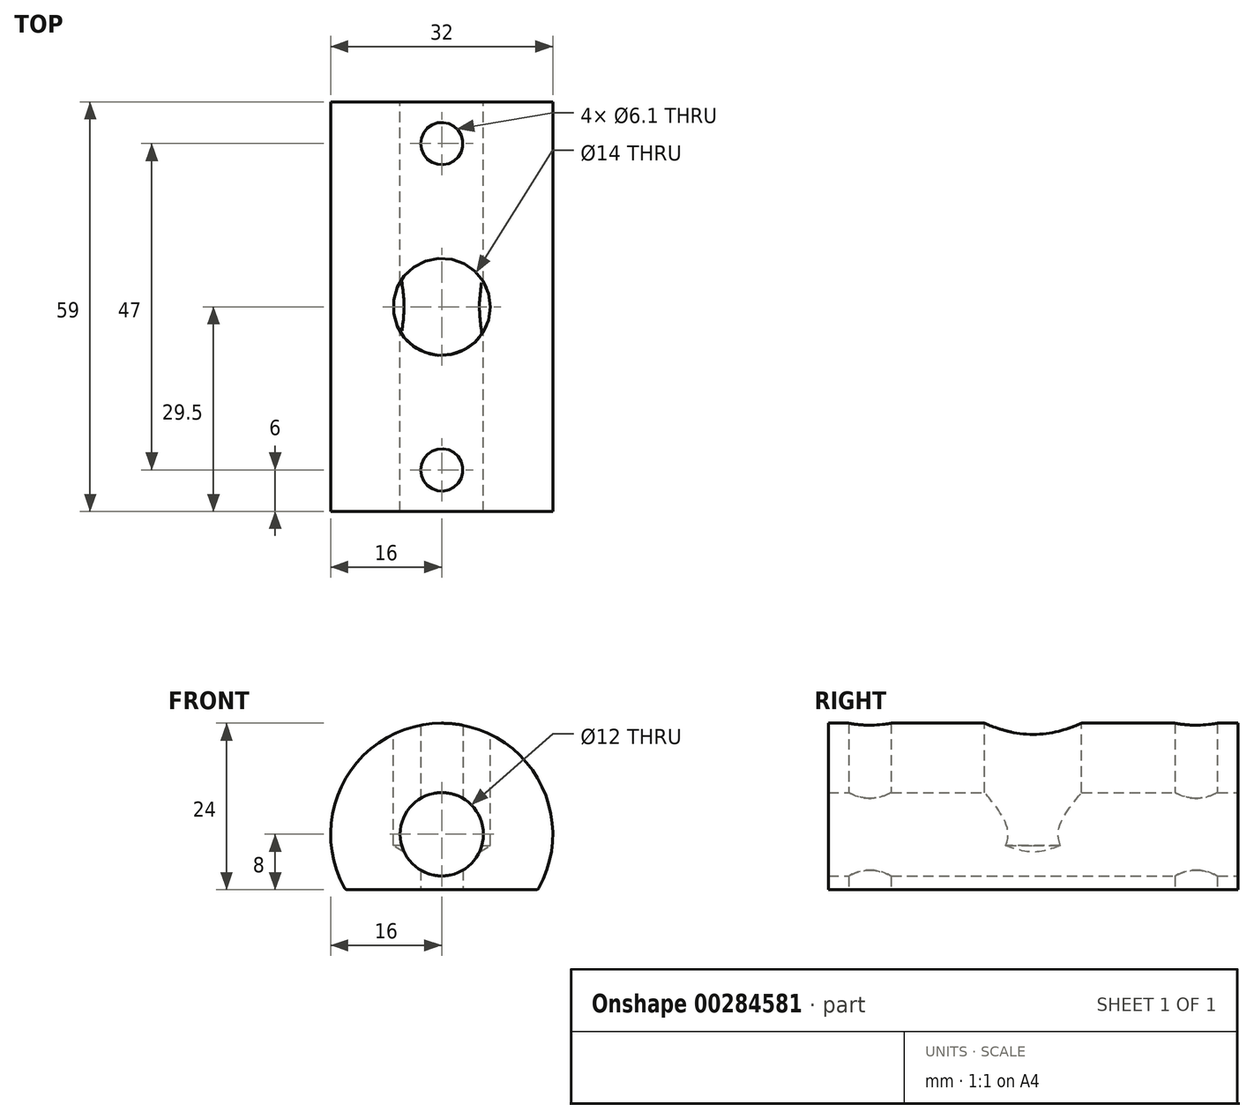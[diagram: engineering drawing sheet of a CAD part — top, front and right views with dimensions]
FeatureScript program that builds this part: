
annotation { "Feature Type Name" : "Feature", "Feature Type Description" : "" }
export const myFeature = defineFeature(function(context is Context, id is Id, definition is map)
    precondition{}
    {
        {
            var Q0;
            Q0=qCreatedBy(makeId("Front.planeOp"),FACE);
            var sketch = newSketch(context, id + "F0", { "sketchPlane" : qUnion([Q0])});
            skArc(sketch, "E0", {"start": v(14, -7.74) * mm, "mid": v(0, 16) * mm, "end": v(-14, -7.74) * mm});
            skCircle(sketch, "E1", {"center": v(0, 0) * mm, "radius": 6 * mm});
            skLineSegment(sketch, "E2", {"start": v(-13.56, -8) * mm, "end": v(13.56, -8) * mm});
            skPoint(sketch, "E3.visualSharp", {"position": v(-13.86, -8) * mm});
            skArc(sketch, "E3.filletArc", {"start": v(-14, -7.74) * mm, "mid": v(-13.82, -7.93) * mm, "end": v(-13.56, -8) * mm});
            skPoint(sketch, "E4.visualSharp", {"position": v(13.86, -8) * mm});
            skArc(sketch, "E4.filletArc", {"start": v(13.56, -8) * mm, "mid": v(13.82, -7.93) * mm, "end": v(14, -7.74) * mm});
            skSolve(sketch);
        }
        {
            var Q0;
            Q0=qSketchRegion(id+"F0",true);
            extrude(context, id + "F1", {"entities" : qUnion([Q0]), "depth" : 59 * mm});
        }
        {
            var Q0;
            Q0=makeQuery(id+"F1.opExtrude","SWEPT_FACE",FACE,{"disambiguationData":[OSD([sQuery(id+"F0.wireOp",EDGE,"E2")])]});
            var sketch = newSketch(context, id + "F2", { "sketchPlane" : qUnion([Q0])});
            skPoint(sketch, "E5", {"position": v(0, 53) * mm});
            skPoint(sketch, "E6", {"position": v(0, 6) * mm});
            skSolve(sketch);
        }
        {
            var Q0;
            Q0=sQuery(id+"F2.wireOp",VERTEX,"E6");
            var Q1;
            Q1=sQuery(id+"F2.wireOp",VERTEX,"E5");
            var Q2;
            Q2=makeQuery(id+"F1.opExtrude","SWEPT_BODY",BODY,{"disambiguationData":[OSD([sQuery(id+"F0.wireOp",EDGE,"E0"),sQuery(id+"F0.wireOp",EDGE,"E1"),sQuery(id+"F0.wireOp",EDGE,"E2"),sQuery(id+"F0.wireOp",EDGE,"E3.filletArc"),sQuery(id+"F0.wireOp",EDGE,"E4.filletArc")])]});
            hole(context, id + "F3", {"style" : HoleStyle.SIMPLE, "endStyle" : HoleEndStyle.THROUGH, "holeDiameter" : 6.1 * mm, "locations" : qUnion([Q0, Q1]), "scope" : qUnion([Q2]), "isTappedThrough" : true});
        }
        {
            var Q0;
            Q0=qCreatedBy(makeId("Top.planeOp"),FACE);
            cPlane(context, id + "F4", {"entities" : qUnion([Q0]), "cplaneType" : CPlaneType.OFFSET, "offset" : 16 * mm, "width" : 150 * mm, "height" : 150 * mm});
        }
        {
            var Q0;
            Q0=qCreatedBy(id+"F4.planeOp",FACE);
            var sketch = newSketch(context, id + "F5", { "sketchPlane" : qUnion([Q0])});
            skPoint(sketch, "E7", {"position": v(0, -29.5) * mm});
            skSolve(sketch);
        }
        {
            var Q0;
            Q0=sQuery(id+"F5.wireOp",VERTEX,"E7");
            var Q1;
            Q1=makeQuery(id+"F1.opExtrude","SWEPT_BODY",BODY,{"disambiguationData":[OSD([sQuery(id+"F0.wireOp",EDGE,"E0"),sQuery(id+"F0.wireOp",EDGE,"E1"),sQuery(id+"F0.wireOp",EDGE,"E2"),sQuery(id+"F0.wireOp",EDGE,"E3.filletArc"),sQuery(id+"F0.wireOp",EDGE,"E4.filletArc")])]});
            hole(context, id + "F6", {"style" : HoleStyle.SIMPLE, "endStyle" : HoleEndStyle.BLIND, "holeDiameter" : 14 * mm, "holeDepth" : 16 * mm, "locations" : qUnion([Q0]), "scope" : qUnion([Q1])});
        }
    });
